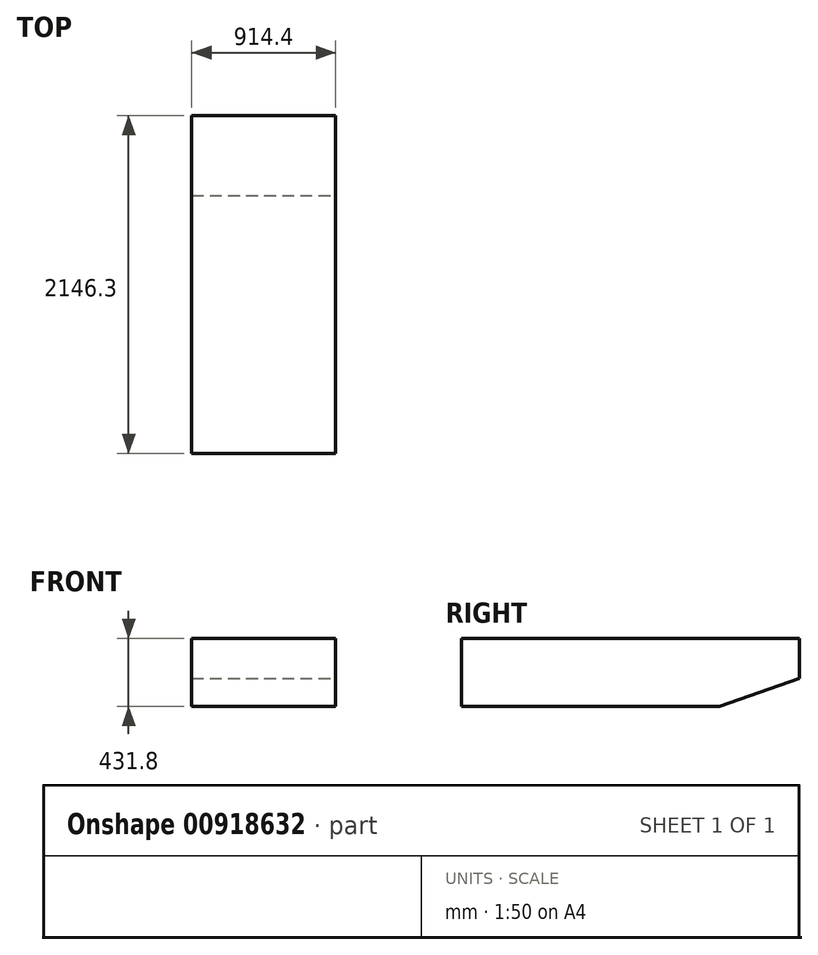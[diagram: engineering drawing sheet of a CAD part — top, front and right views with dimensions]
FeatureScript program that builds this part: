
annotation { "Feature Type Name" : "Feature", "Feature Type Description" : "" }
export const myFeature = defineFeature(function(context is Context, id is Id, definition is map)
    precondition{}
    {
        {
            var Q0;
            Q0=qCreatedBy(makeId("Front.planeOp"),FACE);
            var sketch = newSketch(context, id + "F0", { "sketchPlane" : qUnion([Q0])});
            skLineSegment(sketch, "E0.bottom", {"start": v(-457.2, 215.9) * mm, "end": v(457.2, 215.9) * mm});
            skLineSegment(sketch, "E0.top", {"start": v(-457.2, -215.9) * mm, "end": v(457.2, -215.9) * mm});
            skLineSegment(sketch, "E0.left", {"start": v(-457.2, 215.9) * mm, "end": v(-457.2, -215.9) * mm});
            skLineSegment(sketch, "E0.right", {"start": v(457.2, 215.9) * mm, "end": v(457.2, -215.9) * mm});
            skLineSegment(sketch, "E1", {"start": v(-457.2, 215.9) * mm, "end": v(457.2, -215.9) * mm, "construction": true});
            skSolve(sketch);
        }
        {
            var Q0;
            Q0=makeQuery(id+"F0.imprint","IMPRINT",FACE,{"disambiguationData":[TD([[makeQuery(id+"F0.imprint","IMPRINT",EDGE,{"derivedFrom":sQuery(id+"F0.wireOp",EDGE,"E0.bottom")}),-1.0]])]});
            extrude(context, id + "F1", {"entities" : qUnion([Q0]), "depth" : 2146.3 * mm, "offsetDistance" : 25.4 * mm, "symmetric" : true});
        }
        {
            var Q0;
            Q0=makeQuery(id+"F1.opExtrude","SWEPT_FACE",FACE,{"disambiguationData":[OSD([sQuery(id+"F0.wireOp",EDGE,"E0.right")])]});
            var sketch = newSketch(context, id + "F2", { "sketchPlane" : qUnion([Q0])});
            skLineSegment(sketch, "E2", {"start": v(1073.15, -38.1) * mm, "end": v(1073.15, -215.9) * mm});
            skLineSegment(sketch, "E3", {"start": v(1073.15, -215.9) * mm, "end": v(565.15, -215.9) * mm});
            skLineSegment(sketch, "E4", {"start": v(565.15, -215.9) * mm, "end": v(1073.15, -38.1) * mm});
            skSolve(sketch);
        }
        {
            var Q0;
            Q0=makeQuery(id+"F2.imprint","IMPRINT",FACE,{"disambiguationData":[TD([[makeQuery(id+"F2.imprint","IMPRINT",EDGE,{"derivedFrom":sQuery(id+"F2.wireOp",EDGE,"RXpSDKXg-inJH-Siv3-fzvw-C6r1FnJEwCKR")}),-1.0]])]});
            var Q1;
            Q1=makeQuery(id+"F2.imprint","IMPRINT",FACE,{"disambiguationData":[TD([[makeQuery(id+"F2.imprint","IMPRINT",EDGE,{"derivedFrom":sQuery(id+"F2.wireOp",EDGE,"E2")}),-1.0]])]});
            extrude(context, id + "F3", {"entities" : qUnion([Q0, Q1]), "operationType" : NewBodyOperationType.REMOVE, "endBound" : BoundingType.THROUGH_ALL, "oppositeDirection" : true, "depth" : 25.4 * mm, "offsetDistance" : 25.4 * mm});
        }
    });
